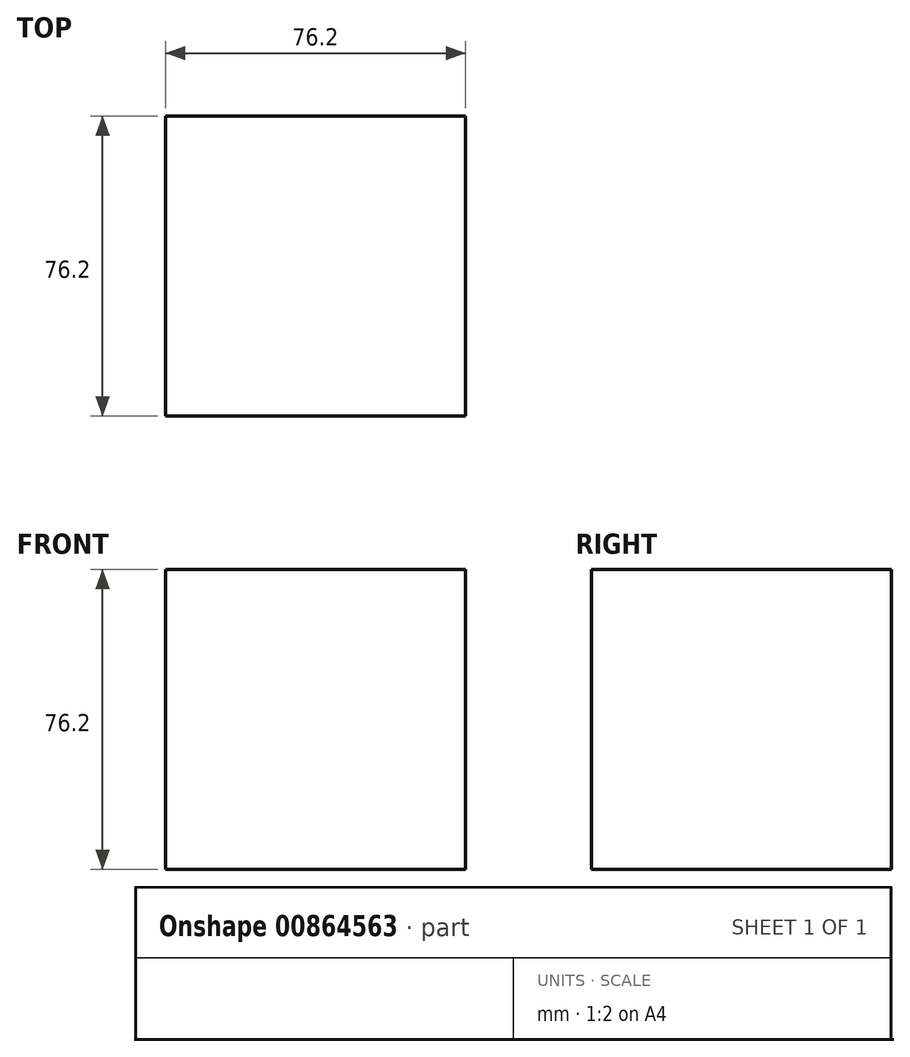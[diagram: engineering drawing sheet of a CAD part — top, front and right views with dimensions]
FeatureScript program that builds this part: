
annotation { "Feature Type Name" : "Feature", "Feature Type Description" : "" }
export const myFeature = defineFeature(function(context is Context, id is Id, definition is map)
    precondition{}
    {
        {
            var Q0;
            Q0=qCreatedBy(makeId("Top.planeOp"),FACE);
            var sketch = newSketch(context, id + "F0", { "sketchPlane" : qUnion([Q0])});
            skLineSegment(sketch, "E0.bottom", {"start": v(-76.2, 76.2) * mm, "end": v(0, 76.2) * mm});
            skLineSegment(sketch, "E0.top", {"start": v(-76.2, 0) * mm, "end": v(0, 0) * mm});
            skLineSegment(sketch, "E0.left", {"start": v(-76.2, 76.2) * mm, "end": v(-76.2, 0) * mm});
            skLineSegment(sketch, "E0.right", {"start": v(0, 76.2) * mm, "end": v(0, 0) * mm});
            skSolve(sketch);
        }
        {
            var Q0;
            Q0=makeQuery(id+"F0.imprint","IMPRINT",FACE,{"disambiguationData":[TD([[makeQuery(id+"F0.imprint","IMPRINT",EDGE,{"derivedFrom":sQuery(id+"F0.wireOp",EDGE,"E0.bottom")}),-1.0]])]});
            extrude(context, id + "F1", {"entities" : qUnion([Q0]), "depth" : 76.2 * mm, "offsetDistance" : 25.4 * mm});
        }
        {
            var Q0;
            Q0=makeQuery(id+"F1.opExtrude","CAP_FACE",FACE,{"disambiguationData":[OSD([sQuery(id+"F0.wireOp",EDGE,"E0.bottom"),sQuery(id+"F0.wireOp",EDGE,"E0.top"),sQuery(id+"F0.wireOp",EDGE,"E0.left"),sQuery(id+"F0.wireOp",EDGE,"E0.right")])],"isStart":false});
            var sketch = newSketch(context, id + "F2", { "sketchPlane" : qUnion([Q0])});
            skSolve(sketch);
        }
    });
